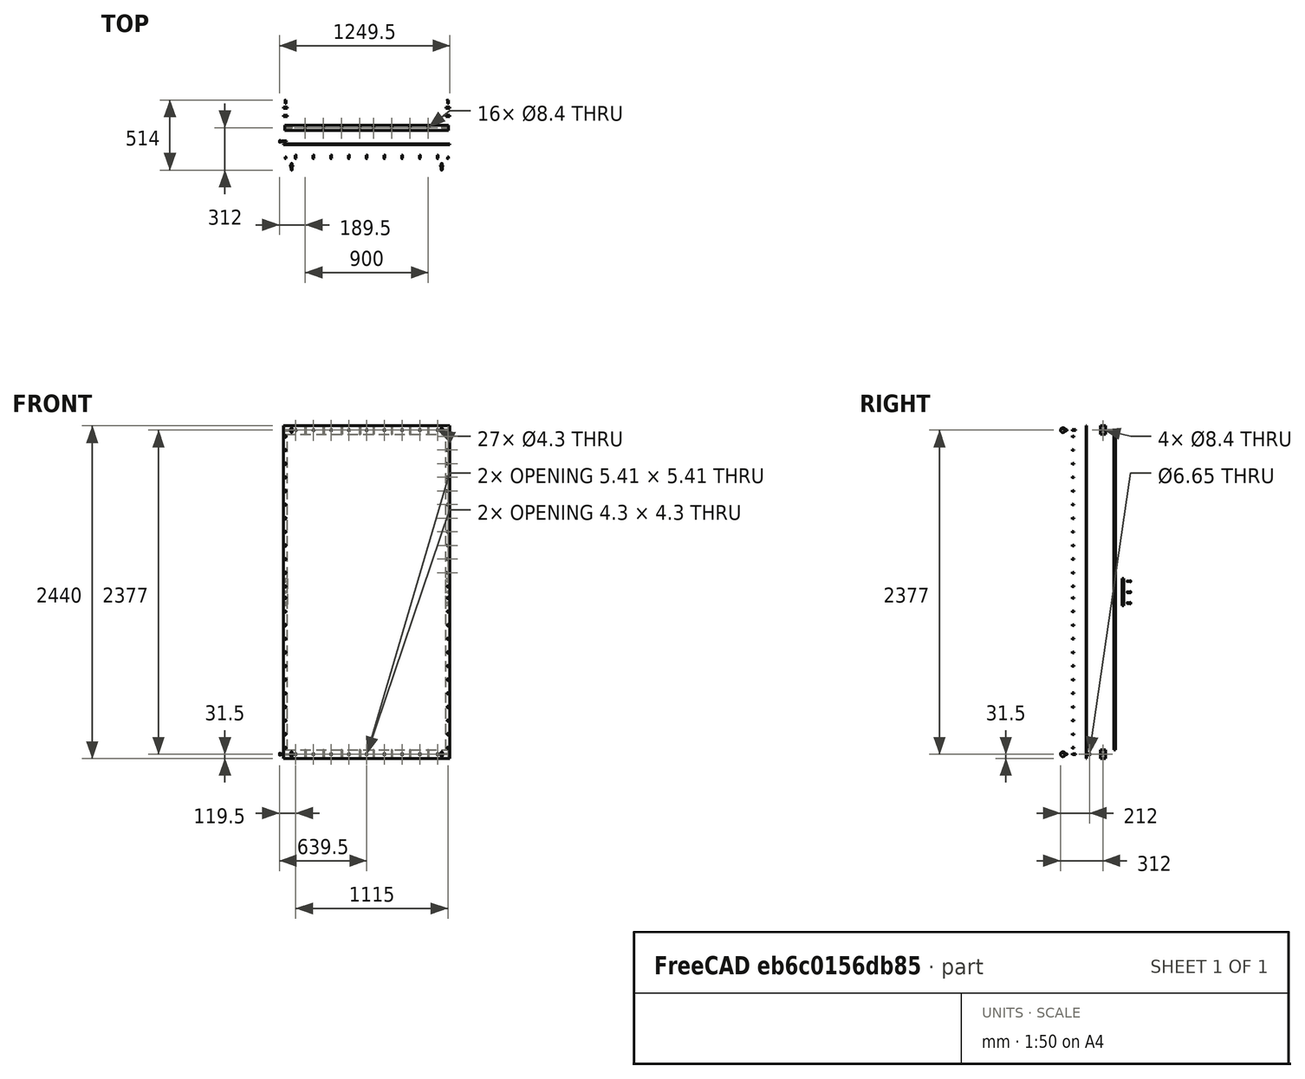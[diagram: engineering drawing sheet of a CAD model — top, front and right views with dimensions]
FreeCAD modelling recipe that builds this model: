
FCSTD DOCUMENT  (FreeCAD 0.21R33771 (Git))
Label: reflector_2024_assembly_exploded
License: All rights reserved
LicenseURL: https://en.wikipedia.org/wiki/All_rights_reserved
objects: Part::FeaturePython×30, Part::Feature×13, App::DocumentObjectGroupPython×10, Part::Compound×5, Part::Mirroring×2, TechDraw::DrawSVGTemplate×2, TechDraw::DrawViewPart×2, TechDraw::DrawPage×2, Spreadsheet::Sheet×1
note: 42 computed .brp shape members not serialized (recipe doc carries the construction recipe); baked Part::Feature solids carry a one-line shape summary decoded from their .brp

FEATURE [Part::FeaturePython] b_reflector_2024_panel_001_  label="reflector_2024_panel_panel_001"  # a2plus imported part (geometry in sourceFile) (typed FeaturePython)
  a2p_Version = 0.4.64
  fixedPosition = true
  objectType = a2pPart
  sourceFile = ./reflector_2024_panel.FCStd
  sourcePart = panel
  subassemblyImport = false
  timeLastImport = 1.71015e+09
  updateColors = true
FEATURE [Part::FeaturePython] b_reflector_2024_listello_001_  label="reflector_2024_listello_Body_001"  # a2plus imported part (geometry in sourceFile) (typed FeaturePython)
  Placement = pos=(-595,205,0) rot=(0,0,1;0rad)
  a2p_Version = 0.4.64
  fixedPosition = false
  objectType = a2pPart
  sourceFile = ./reflector_2024_listello.FCStd
  sourcePart = Body
  subassemblyImport = false
  timeLastImport = 1.71015e+09
  updateColors = true
  expr: .Placement.Base.x = -610 + 15
FEATURE [Part::FeaturePython] b_reflector_2024_listello_Body_001_  label="reflector_2024_listello_Body_002"  # a2plus imported part (geometry in sourceFile) (typed FeaturePython)
  Placement = pos=(595,205,0) rot=(0,0,1;0rad)
  a2p_Version = 0.4.64
  fixedPosition = false
  objectType = a2pPart
  sourceFile = ./reflector_2024_listello.FCStd
  sourcePart = Body
  subassemblyImport = false
  timeLastImport = 1.71015e+09
  updateColors = true
  expr: .Placement.Base.x = 610 - 15
FEATURE [Part::FeaturePython] Screw006  label="M6x12-Screw"  # Fasteners workbench fastener (typed FeaturePython)
  Placement = pos=(595,-7,1142) rot=(1,0,0;1.5708rad)
  diameter = 8
  invert = false
  leftHanded = false
  length = 2
  lengthCustom = 12
  matchOuter = false
  offset = 0
  thread = false
  type = 73
  expr: .Placement.Base.x = 1220 / 2 - 30 / 2
  expr: .Placement.Base.y = -7
  expr: .Placement.Base.z = 1220 - 63 - 15
FEATURE [Part::FeaturePython] Array004  # Draft array (typed FeaturePython)
  AlwaysSyncPlacement = false
  Angle = 360
  ArrayType = 0
  Axis = (0,0,1)
  Base = -> Screw006
  Center = (0,0,0)
  Count = 12
  ExpandArray = false
  Fuse = false
  IntervalAxis = (0,0,0)
  IntervalX = (100,0,0)
  IntervalY = (0,100,0)
  IntervalZ = (0,0,-100)
  NumberCircles = 3
  NumberPolar = 5
  NumberX = 1
  NumberY = 1
  NumberZ = 12
  PlacementList = 12 placements: arithmetic series from (595,-7,1142) step (0,0,-100) to (595,-7,42)
  RadialDistance = 50
  ScaleList = (12) [(1,1,1),(1,1,1),(1,1,1),(1,1,1),(1,1,1),(1,1,1),(1,1,1),(1,1,1),(1,1,1),(1,1,1),(1,1,1),(1,1,1)]
  Symmetry = 1
  TangentialDistance = 25
FEATURE [Part::FeaturePython] Screw007  label="M6x12-Screw006"  # Fasteners workbench fastener (typed FeaturePython)
  Placement = pos=(595,-7,-1142) rot=(1,0,0;1.5708rad)
  diameter = 8
  invert = false
  leftHanded = false
  length = 2
  lengthCustom = 12
  matchOuter = false
  offset = 0
  thread = false
  type = 73
  expr: .Placement.Base.x = 1220 / 2 - 30 / 2
  expr: .Placement.Base.y = -7
  expr: .Placement.Base.z = -(1220 - 63 - 15)
FEATURE [Part::FeaturePython] Array005  # Draft array (typed FeaturePython)
  AlwaysSyncPlacement = false
  Angle = 360
  ArrayType = 0
  Axis = (0,0,1)
  Base = -> Screw007
  Center = (0,0,0)
  Count = 12
  ExpandArray = false
  Fuse = false
  IntervalAxis = (0,0,0)
  IntervalX = (100,0,0)
  IntervalY = (0,100,0)
  IntervalZ = (0,0,100)
  NumberCircles = 3
  NumberPolar = 5
  NumberX = 1
  NumberY = 1
  NumberZ = 12
  PlacementList = 12 placements: arithmetic series from (595,-7,-1142) step (0,0,100) to (595,-7,-42)
  RadialDistance = 50
  ScaleList = (12) [(1,1,1),(1,1,1),(1,1,1),(1,1,1),(1,1,1),(1,1,1),(1,1,1),(1,1,1),(1,1,1),(1,1,1),(1,1,1),(1,1,1)]
  Symmetry = 1
  TangentialDistance = 25
FEATURE [Part::FeaturePython] Screw008  label="M6x12-Screw007"  # Fasteners workbench fastener (typed FeaturePython)
  Placement = pos=(-595,-7,1142) rot=(1,0,0;1.5708rad)
  diameter = 8
  invert = false
  leftHanded = false
  length = 2
  lengthCustom = 12
  matchOuter = false
  offset = 0
  thread = false
  type = 73
  expr: .Placement.Base.x = -(1220 / 2 - 30 / 2)
  expr: .Placement.Base.y = -7
  expr: .Placement.Base.z = 1220 - 63 - 15
FEATURE [Part::FeaturePython] Array006  # Draft array (typed FeaturePython)
  AlwaysSyncPlacement = false
  Angle = 360
  ArrayType = 0
  Axis = (0,0,1)
  Base = -> Screw008
  Center = (0,0,0)
  Count = 12
  ExpandArray = false
  Fuse = false
  IntervalAxis = (0,0,0)
  IntervalX = (100,0,0)
  IntervalY = (0,100,0)
  IntervalZ = (0,0,-100)
  NumberCircles = 3
  NumberPolar = 5
  NumberX = 1
  NumberY = 1
  NumberZ = 12
  PlacementList = 12 placements: arithmetic series from (-595,-7,1142) step (0,0,-100) to (-595,-7,42)
  RadialDistance = 50
  ScaleList = (12) [(1,1,1),(1,1,1),(1,1,1),(1,1,1),(1,1,1),(1,1,1),(1,1,1),(1,1,1),(1,1,1),(1,1,1),(1,1,1),(1,1,1)]
  Symmetry = 1
  TangentialDistance = 25
FEATURE [Part::FeaturePython] Screw009  label="M6x12-Screw008"  # Fasteners workbench fastener (typed FeaturePython)
  Placement = pos=(-595,-7,-1142) rot=(1,0,0;1.5708rad)
  diameter = 8
  invert = false
  leftHanded = false
  length = 2
  lengthCustom = 12
  matchOuter = false
  offset = 0
  thread = false
  type = 73
  expr: .Placement.Base.x = -(1220 / 2 - 30 / 2)
  expr: .Placement.Base.y = -7
  expr: .Placement.Base.z = -(1220 - 63 - 15)
FEATURE [Part::FeaturePython] Array007  # Draft array (typed FeaturePython)
  AlwaysSyncPlacement = false
  Angle = 360
  ArrayType = 0
  Axis = (0,0,1)
  Base = -> Screw009
  Center = (0,0,0)
  Count = 12
  ExpandArray = false
  Fuse = false
  IntervalAxis = (0,0,0)
  IntervalX = (100,0,0)
  IntervalY = (0,100,0)
  IntervalZ = (0,0,100)
  NumberCircles = 3
  NumberPolar = 5
  NumberX = 1
  NumberY = 1
  NumberZ = 12
  PlacementList = 12 placements: arithmetic series from (-595,-7,-1142) step (0,0,100) to (-595,-7,-42)
  RadialDistance = 50
  ScaleList = (12) [(1,1,1),(1,1,1),(1,1,1),(1,1,1),(1,1,1),(1,1,1),(1,1,1),(1,1,1),(1,1,1),(1,1,1),(1,1,1),(1,1,1)]
  Symmetry = 1
  TangentialDistance = 25
FEATURE [Part::FeaturePython] Screw010  label="M6x25-Screw006"  # Fasteners workbench fastener (typed FeaturePython)
  Placement = pos=(0,-7,1188.5) rot=(1,0,0;1.5708rad)
  diameter = 8
  invert = false
  leftHanded = false
  length = 6
  lengthCustom = 25
  matchOuter = false
  offset = 0
  thread = false
  type = 73
FEATURE [Part::FeaturePython] Array  # Draft array (typed FeaturePython)
  AlwaysSyncPlacement = false
  Angle = 360
  ArrayType = 0
  Axis = (0,0,1)
  Base = -> Screw010
  Center = (0,0,0)
  Count = 5
  ExpandArray = false
  Fuse = false
  IntervalAxis = (0,0,0)
  IntervalX = (130,0,0)
  IntervalY = (0,100,0)
  IntervalZ = (0,0,100)
  NumberCircles = 3
  NumberPolar = 5
  NumberX = 5
  NumberY = 1
  NumberZ = 1
  PlacementList = 5 placements: arithmetic series from (0,-7,1188.5) step (130,0,0) to (520,-7,1188.5)
  RadialDistance = 50
  ScaleList = (5) [(1,1,1),(1,1,1),(1,1,1),(1,1,1),(1,1,1)]
  Symmetry = 1
  TangentialDistance = 25
FEATURE [Part::Compound] Compound001  label="screws_listelli"
  Links = -> [Array004,Array005,Array006,Array007]
  Placement = pos=(0,-100,0) rot=(0,0,1;0rad)
FEATURE [Part::FeaturePython] Array008  # Draft array (typed FeaturePython)
  AlwaysSyncPlacement = false
  Angle = 360
  ArrayType = 0
  Axis = (0,0,1)
  Base = -> Screw010
  Center = (0,0,0)
  Count = 5
  ExpandArray = false
  Fuse = false
  IntervalAxis = (0,0,0)
  IntervalX = (-130,0,0)
  IntervalY = (0,100,0)
  IntervalZ = (0,0,100)
  NumberCircles = 3
  NumberPolar = 5
  NumberX = 5
  NumberY = 1
  NumberZ = 1
  PlacementList = 5 placements: arithmetic series from (0,-7,1188.5) step (-130,0,0) to (-520,-7,1188.5)
  RadialDistance = 50
  ScaleList = (5) [(1,1,1),(1,1,1),(1,1,1),(1,1,1),(1,1,1)]
  Symmetry = 1
  TangentialDistance = 25
FEATURE [Part::FeaturePython] Screw011  label="M6x25-Screw007"  # Fasteners workbench fastener (typed FeaturePython)
  Placement = pos=(0,-7,-1188.5) rot=(1,0,0;1.5708rad)
  diameter = 8
  invert = false
  leftHanded = false
  length = 6
  lengthCustom = 25
  matchOuter = false
  offset = 0
  thread = false
  type = 73
  expr: .Placement.Base.z = -1188.5 mm
FEATURE [Part::FeaturePython] Array009  # Draft array (typed FeaturePython)
  AlwaysSyncPlacement = false
  Angle = 360
  ArrayType = 0
  Axis = (0,0,1)
  Base = -> Screw011
  Center = (0,0,0)
  Count = 5
  ExpandArray = false
  Fuse = false
  IntervalAxis = (0,0,0)
  IntervalX = (130,0,0)
  IntervalY = (0,100,0)
  IntervalZ = (0,0,100)
  NumberCircles = 3
  NumberPolar = 5
  NumberX = 5
  NumberY = 1
  NumberZ = 1
  PlacementList = 5 placements: arithmetic series from (0,-7,-1188.5) step (130,0,0) to (520,-7,-1188.5)
  RadialDistance = 50
  ScaleList = (5) [(1,1,1),(1,1,1),(1,1,1),(1,1,1),(1,1,1)]
  Symmetry = 1
  TangentialDistance = 25
FEATURE [Part::FeaturePython] Array010  # Draft array (typed FeaturePython)
  AlwaysSyncPlacement = false
  Angle = 360
  ArrayType = 0
  Axis = (0,0,1)
  Base = -> Screw011
  Center = (0,0,0)
  Count = 5
  ExpandArray = false
  Fuse = false
  IntervalAxis = (0,0,0)
  IntervalX = (-130,0,0)
  IntervalY = (0,100,0)
  IntervalZ = (0,0,100)
  NumberCircles = 3
  NumberPolar = 5
  NumberX = 5
  NumberY = 1
  NumberZ = 1
  PlacementList = 5 placements: arithmetic series from (0,-7,-1188.5) step (-130,0,0) to (-520,-7,-1188.5)
  RadialDistance = 50
  ScaleList = (5) [(1,1,1),(1,1,1),(1,1,1),(1,1,1),(1,1,1)]
  Symmetry = 1
  TangentialDistance = 25
FEATURE [Part::Compound] Compound  label="screws_battens"
  Links = -> [Array,Array008,Array009,Array010]
  Placement = pos=(0,-100,0) rot=(0,0,1;0rad)
FEATURE [Part::Feature] Part__Feature  label="LIFTING EYE BOLT - M8 - DIN 580_1"
  Placement = pos=(550,-25,1188.5) rot=(0.707107,0,-0.707107;3.14159rad)
  shape: bbox 21.03 x 49.35 x 36.93 mm, 59 faces (baked)
  expr: .Placement.Base.x = 610 - 60
  expr: .Placement.Base.z = 1220 - 63 / 2
FEATURE [Part::Feature] Part__Feature001  label="LIFTING EYE BOLT - M8 - DIN 580_2"
  Placement = pos=(-550,-25,1188.5) rot=(0.707107,0,-0.707107;3.14159rad)
  shape: bbox 21.03 x 49.35 x 36.93 mm, 59 faces (baked)
  expr: .Placement.Base.x = -(610 - 60)
  expr: .Placement.Base.z = 1220 - 63 / 2
FEATURE [Part::Feature] Part__Feature002  label="LIFTING EYE BOLT - M8 - DIN 580_3"
  Placement = pos=(550,-25,-1188.5) rot=(0.707107,0,-0.707107;3.14159rad)
  shape: bbox 21.03 x 49.35 x 36.93 mm, 59 faces (baked)
  expr: .Placement.Base.x = 610 - 60
  expr: .Placement.Base.z = -(1220 - 63 / 2)
FEATURE [Part::Feature] Part__Feature003  label="LIFTING EYE BOLT - M8 - DIN 580_4"
  Placement = pos=(-550,-25,-1188.5) rot=(0.707107,0,-0.707107;3.14159rad)
  shape: bbox 21.03 x 49.35 x 36.93 mm, 59 faces (baked)
  expr: .Placement.Base.x = -(610 - 60)
  expr: .Placement.Base.z = -(1220 - 63 / 2)
FEATURE [Part::Compound] Compound002  label="eye_bolts"
  Links = -> [Part__Feature,Part__Feature001,Part__Feature002,Part__Feature003]
  Placement = pos=(0,-150,0) rot=(0,0,1;0rad)
FEATURE [Part::FeaturePython] b_reflector_2024_listello_handle_001_  label="reflector_2024_listello_handle_001"  # a2plus imported part (geometry in sourceFile) (typed FeaturePython)
  Placement = pos=(595,270,1.1e-13) rot=(0,0,1;0rad)
  a2p_Version = 0.4.64
  fixedPosition = false
  objectType = a2pPart
  sourceFile = ./reflector_2024_listello_handle.FCStd
  subassemblyImport = false
  timeLastImport = 1709987877
  updateColors = true
  expr: .Placement.Base.x = 610 - 15
FEATURE [Part::FeaturePython] b_reflector_2024_listello_handle_001_001  label="reflector_2024_listello_handle_002"  # a2plus imported part (geometry in sourceFile) (typed FeaturePython)
  Placement = pos=(-595,270,1.1e-13) rot=(0,0,1;0rad)
  a2p_Version = 0.4.64
  fixedPosition = false
  objectType = a2pPart
  sourceFile = ./reflector_2024_listello_handle.FCStd
  subassemblyImport = false
  timeLastImport = 1709987877
  updateColors = true
  expr: .Placement.Base.x = -610 + 15
FEATURE [Part::FeaturePython] Screw  label="M6x25-Screw"  # Fasteners workbench fastener (typed FeaturePython)
  Placement = pos=(595,21,0) rot=(-1,0,0;1.5708rad)
  diameter = 8
  invert = false
  leftHanded = false
  length = 6
  lengthCustom = 25
  matchOuter = false
  offset = 0
  thread = false
  type = 73
  expr: .Placement.Base.x = 610 - 15
FEATURE [Part::FeaturePython] Screw012  label="M6x25-Screw001"  # Fasteners workbench fastener (typed FeaturePython)
  Placement = pos=(595,21,80) rot=(-1,0,0;1.5708rad)
  diameter = 8
  invert = false
  leftHanded = false
  length = 6
  lengthCustom = 25
  matchOuter = false
  offset = 0
  thread = false
  type = 73
  expr: .Placement.Base.x = 610 - 15
FEATURE [Part::FeaturePython] Screw013  label="M6x25-Screw002"  # Fasteners workbench fastener (typed FeaturePython)
  Placement = pos=(595,21,-80) rot=(-1,0,0;1.5708rad)
  diameter = 8
  invert = false
  leftHanded = false
  length = 6
  lengthCustom = 25
  matchOuter = false
  offset = 0
  thread = false
  type = 73
  expr: .Placement.Base.x = 610 - 15
FEATURE [Part::FeaturePython] Screw014  label="M6x25-Screw003"  # Fasteners workbench fastener (typed FeaturePython)
  Placement = pos=(-595,21,0) rot=(-1,0,0;1.5708rad)
  diameter = 8
  invert = false
  leftHanded = false
  length = 6
  lengthCustom = 25
  matchOuter = false
  offset = 0
  thread = false
  type = 73
  expr: .Placement.Base.x = -610 + 15
FEATURE [Part::FeaturePython] Screw015  label="M6x25-Screw004"  # Fasteners workbench fastener (typed FeaturePython)
  Placement = pos=(-595,21,80) rot=(-1,0,0;1.5708rad)
  diameter = 8
  invert = false
  leftHanded = false
  length = 6
  lengthCustom = 25
  matchOuter = false
  offset = 0
  thread = false
  type = 73
  expr: .Placement.Base.x = -610 + 15
FEATURE [Part::FeaturePython] Screw016  label="M6x25-Screw005"  # Fasteners workbench fastener (typed FeaturePython)
  Placement = pos=(-595,21,-80) rot=(-1,0,0;1.5708rad)
  diameter = 8
  invert = false
  leftHanded = false
  length = 6
  lengthCustom = 25
  matchOuter = false
  offset = 0
  thread = false
  type = 73
  expr: .Placement.Base.x = -610 + 15
FEATURE [Part::Compound] Compound003  label="screws_handles"
  Links = -> [Screw,Screw012,Screw013,Screw014,Screw015,Screw016]
  Placement = pos=(0,300,0) rot=(0,0,1;0rad)
FEATURE [Part::FeaturePython] b_reflector_2024_timber_001_  label="reflector_2024_timber_001"  # a2plus imported part (geometry in sourceFile) (typed FeaturePython)
  Placement = pos=(0,19,1188.5) rot=(0,0,1;0rad)
  a2p_Version = 0.4.64
  fixedPosition = false
  objectType = a2pPart
  sourceFile = ./reflector_2024_timber.FCStd
  subassemblyImport = false
  timeLastImport = 1.71015e+09
  updateColors = true
  expr: .Placement.Base.y = 38 / 2
FEATURE [Part::FeaturePython] b_reflector_2024_timber_001_001  label="reflector_2024_timber_002"  # a2plus imported part (geometry in sourceFile) (typed FeaturePython)
  Placement = pos=(1.1e-13,19,-1188.5) rot=(0,0,1;0rad)
  a2p_Version = 0.4.64
  fixedPosition = false
  objectType = a2pPart
  sourceFile = ./reflector_2024_timber.FCStd
  subassemblyImport = false
  timeLastImport = 1.71015e+09
  updateColors = true
  expr: .Placement.Base.y = 38 / 2
FEATURE [Part::FeaturePython] ScrewTap  label="M8x35-ScrewTap"  # Fasteners workbench fastener (typed FeaturePython)
  Placement = pos=(622,19,-1188.5) rot=(0,1,0;1.5708rad)
  diameter = 9
  diameterCustom = 6
  invert = false
  leftHanded = false
  length = 35
  matchOuter = false
  offset = 0
  pitchCustom = 1
  thread = false
  type = 2
  expr: .Placement.Base.y = 38 / 2
  expr: .Placement.Base.z = -1220 + 63 / 2
FEATURE [Part::Mirroring] Mirror  label="M8x35-ScrewTap (mirrored)"
  Base = (0,0,0)
  Normal = (1,0,0)
  Source = -> ScrewTap
FEATURE [Part::FeaturePython] b_reflector_2024_base_001_  label="reflector_2024_base_001"  # a2plus imported part (geometry in sourceFile) (typed FeaturePython)
  Placement = pos=(0,19,-1244.67) rot=(0,0,1;0rad)
  a2p_Version = 0.4.64
  fixedPosition = false
  objectType = a2pPart
  sourceFile = .\reflector_2024_base.FCStd
  subassemblyImport = true
  timeLastImport = 1.71052e+09
  updateColors = true
FEATURE [Part::FeaturePython] Nut  label="M8-Nut"  # Fasteners workbench fastener (typed FeaturePython)
  Placement = pos=(632,19,-1188.5) rot=(0,1,0;1.5708rad)
  diameter = 3
  invert = false
  leftHanded = false
  matchOuter = false
  offset = 0
  thread = false
  type = 32
  expr: .Placement.Base.y = 38 / 2
  expr: .Placement.Base.z = -1220 + 63 / 2
FEATURE [Part::Mirroring] Mirror001  label="M8-Nut (mirrored)"
  Base = (0,0,0)
  Normal = (1,0,0)
  Source = -> Nut
FEATURE [Part::Compound] Compound004  label="timber_battens"
  Links = -> [b_reflector_2024_timber_001_,b_reflector_2024_timber_001_001]
  Placement = pos=(5.5e-14,100,0) rot=(0,0,1;0rad)
FEATURE [Spreadsheet::Sheet] _PARTSLIST_  label="#PARTSLIST#"
  cells = A1='POS; B1='QTY; C1='IDENTNO; D1='DESCRIPTION; E1='SUPPLIER; F1='SUPP.IDENTNO; G1='SUPP.DESCRIPTION; H1='(FILENAME); A2=1; B2=1; C2='*; D2='*; E2='*; F2='*; G2='*; H2='reflector_2024_panel.FCStd; A3=2; B3=2; C3='*; D3='*; E3='*; F3='*; G3='*; H3='reflector_2024_listello.FCStd; A4=3; B4=2; C4='*; D4='*; E4='*; F4='*; G4='*; H4='reflector_2024_listello_handle.FCStd; A5=4; B5=2; C5='*; D5='*; E5='*; F5='*; G5='*; H5='reflector_2024_timber.FCStd; A6=5; B6=1; C6='*; D6='*; E6='*; F6='*; G6='*; H6='reflector_2024_timber_base.FCStd; A7=6; B7=2; C7='*; D7='*; E7='*; F7='*; G7='*; H7='reflector_2024_timber_half.FCStd; A8=7; B8=2; C8='*; D8='*; E8='*; F8='*; G8='*; H8='L_corner.FCStd
FEATURE [Part::Feature] trajectory_line
  shape: bbox 2e-07 x 150 x 2e-07 mm, 0 faces, 0 solids (baked)
FEATURE [App::DocumentObjectGroupPython] SimpleGroup  label="eye_bolts001"  # scripted group (container) (typed FeaturePython)
  AnimationStepTime = 0
  AnimationSteps = 150
  Distance = 150
  Group = -> [trajectory_line]
  Revolutions = 0
  dir_vectors = (1) [(0,-1,0)]
  rot_centers = (1) [(-544.288,-14.0115,-1188.5)]
  rot_vectors = (1) [(0,-1,0)]
FEATURE [Part::Feature] trajectory_line001
  shape: bbox 2e-07 x 100 x 2e-07 mm, 0 faces, 0 solids (baked)
FEATURE [App::DocumentObjectGroupPython] SimpleGroup001  label="screws_battens001"  # scripted group (container) (typed FeaturePython)
  AnimationStepTime = 0
  AnimationSteps = 100
  Distance = 100
  Group = -> [trajectory_line001]
  Revolutions = 0
  dir_vectors = (1) [(0,-1,0)]
  rot_centers = (1) [(130,-7,1188.5)]
  rot_vectors = (1) [(0,-1,0)]
FEATURE [Part::Feature] trajectory_line002
  shape: bbox 2e-07 x 100 x 2e-07 mm, 0 faces, 0 solids (baked)
FEATURE [App::DocumentObjectGroupPython] SimpleGroup002  label="timber_battens001"  # scripted group (container) (typed FeaturePython)
  AnimationStepTime = 0
  AnimationSteps = 100
  Distance = 100
  Group = -> [trajectory_line002]
  Revolutions = 0
  dir_vectors = (1) [(5.5e-16,1,-6e-17)]
  rot_centers = (1) [(1.57019e-13,38,1188.5)]
  rot_vectors = (1) [(5.5e-16,1,-6e-17)]
FEATURE [Part::Feature] trajectory_line003
  shape: bbox 2e-07 x 300 x 2e-07 mm, 0 faces, 0 solids (baked)
FEATURE [App::DocumentObjectGroupPython] SimpleGroup009  label="screws_handles001"  # scripted group (container) (typed FeaturePython)
  AnimationStepTime = 0
  AnimationSteps = 300
  Distance = 300
  Group = -> [trajectory_line003]
  Revolutions = 0
  dir_vectors = (1) [(0,1,0)]
  rot_centers = (1) [(595,21,6.37621e-16)]
  rot_vectors = (1) [(0,1,0)]
FEATURE [Part::Feature] trajectory_line004
  shape: bbox 2e-07 x 250 x 2e-07 mm, 0 faces, 0 solids (baked)
FEATURE [App::DocumentObjectGroupPython] SimpleGroup008  label="handle_L"  # scripted group (container) (typed FeaturePython)
  AnimationStepTime = 0
  AnimationSteps = 250
  Distance = 250
  Group = -> [trajectory_line004]
  Revolutions = 0
  dir_vectors = (1) [(0,1,4.4e-16)]
  rot_centers = (1) [(-595,20,-3.88578e-16)]
  rot_vectors = (1) [(0,1,4.4e-16)]
FEATURE [Part::Feature] trajectory_line005
  shape: bbox 2e-07 x 250 x 2e-07 mm, 0 faces, 0 solids (baked)
FEATURE [App::DocumentObjectGroupPython] SimpleGroup007  label="handle_R"  # scripted group (container) (typed FeaturePython)
  AnimationStepTime = 0
  AnimationSteps = 250
  Distance = 250
  Group = -> [trajectory_line005]
  Revolutions = 0
  dir_vectors = (1) [(0,1,4.4e-16)]
  rot_centers = (1) [(-595,20,-3.88578e-16)]
  rot_vectors = (1) [(0,1,4.4e-16)]
FEATURE [Part::Feature] trajectory_line006
  shape: bbox 2e-07 x 100 x 2e-07 mm, 0 faces, 0 solids (baked)
FEATURE [App::DocumentObjectGroupPython] SimpleGroup003  label="screws_listelli001"  # scripted group (container) (typed FeaturePython)
  AnimationStepTime = 0
  AnimationSteps = 100
  Distance = 100
  Group = -> [trajectory_line006]
  Revolutions = 0
  dir_vectors = (1) [(0,-1,2.22045e-16)]
  rot_centers = (1) [(-595,-7,-742)]
  rot_vectors = (1) [(0,-1,2.22045e-16)]
FEATURE [Part::Feature] trajectory_line007
  shape: bbox 2e-07 x 200 x 2e-07 mm, 0 faces, 0 solids (baked)
FEATURE [App::DocumentObjectGroupPython] SimpleGroup004  label="listello_R"  # scripted group (container) (typed FeaturePython)
  AnimationStepTime = 0
  AnimationSteps = 200
  Distance = 200
  Group = -> [trajectory_line007]
  Revolutions = 0
  dir_vectors = (1) [(0,1,0)]
  rot_centers = (1) [(-595,10,7.57912e-15)]
  rot_vectors = (1) [(0,1,0)]
FEATURE [Part::Feature] trajectory_line008
  shape: bbox 2e-07 x 200 x 2e-07 mm, 0 faces, 0 solids (baked)
FEATURE [App::DocumentObjectGroupPython] SimpleGroup005  label="listello_L"  # scripted group (container) (typed FeaturePython)
  AnimationStepTime = 0
  AnimationSteps = 200
  Distance = 200
  Group = -> [trajectory_line008]
  Revolutions = 0
  dir_vectors = (1) [(0,1,0)]
  rot_centers = (1) [(-595,10,7.57912e-15)]
  rot_vectors = (1) [(0,1,0)]
FEATURE [App::DocumentObjectGroupPython] ExplodedAssembly  label="reflector"  # scripted group (container) (typed FeaturePython)
  AnimationStep = 0
  CurrentTrajectory = -1
  Group = -> [SimpleGroup,SimpleGroup001,SimpleGroup002,SimpleGroup009,SimpleGroup008,SimpleGroup007,SimpleGroup003,SimpleGroup004,SimpleGroup005]
  InAnimation = false
  RemoveAllTrajectories = false
  ResetAnimation = false
FEATURE [TechDraw::DrawSVGTemplate] Template001
  Height = 297
  Orientation = 0
  Template = <userpath>/OneDrive - Arup/Jesmond/Program Files/FreeCAD 0.21/data/Mod/TechDraw/Templates/A4_Portrait_blank.svg
  Width = 210
FEATURE [TechDraw::DrawViewPart] View
  CoarseView = false
  Direction = (0.57735,-0.57735,0.57735)
  Focus = 100
  HardHidden = false
  IsoCount = 0
  IsoHidden = false
  IsoVisible = false
  LockPosition = false
  Perspective = false
  Rotation = 0
  Scale = 0.1
  ScaleType = 2
  ScrubCount = 0
  SeamHidden = false
  SeamVisible = false
  SmoothHidden = false
  SmoothVisible = true
  Source = -> [b_reflector_2024_panel_001_,b_reflector_2024_listello_001_,b_reflector_2024_listello_Body_001_,Compound,Compound001,Compound002,b_reflector_2024_listello_handle_001_,b_reflector_2024_listello_handle_001_001,Compound003,Compound004]
  X = 108.253
  XDirection = (0.707107,0.707107,0)
  Y = 151.371
FEATURE [TechDraw::DrawPage] Page001  label="reflector_exploded_front"
  KeepUpdated = true
  NextBalloonIndex = 1
  ProjectionType = 0
  Template = -> Template001
  Views = -> [View]
FEATURE [TechDraw::DrawSVGTemplate] Template002
  Height = 297
  Orientation = 0
  Template = <userpath>/OneDrive - Arup/Jesmond/Program Files/FreeCAD 0.21/data/Mod/TechDraw/Templates/A4_Portrait_blank.svg
  Width = 210
FEATURE [TechDraw::DrawViewPart] View001
  CoarseView = false
  Direction = (-0.57735,0.57735,0.57735)
  Focus = 100
  HardHidden = false
  IsoCount = 0
  IsoHidden = false
  IsoVisible = false
  LockPosition = false
  Perspective = false
  Rotation = 0
  Scale = 0.1
  ScaleType = 2
  ScrubCount = 0
  SeamHidden = false
  SeamVisible = false
  SmoothHidden = false
  SmoothVisible = true
  Source = -> [b_reflector_2024_panel_001_,b_reflector_2024_listello_001_,b_reflector_2024_listello_Body_001_,Compound,Compound001,Compound002,b_reflector_2024_listello_handle_001_,b_reflector_2024_listello_handle_001_001,Compound003,Compound004]
  X = 105
  XDirection = (-0.707107,-0.707107,0)
  Y = 148.5
FEATURE [TechDraw::DrawPage] Page002  label="reflector_exploded_back"
  KeepUpdated = true
  NextBalloonIndex = 1
  ProjectionType = 0
  Template = -> Template002
  Views = -> [View001]
